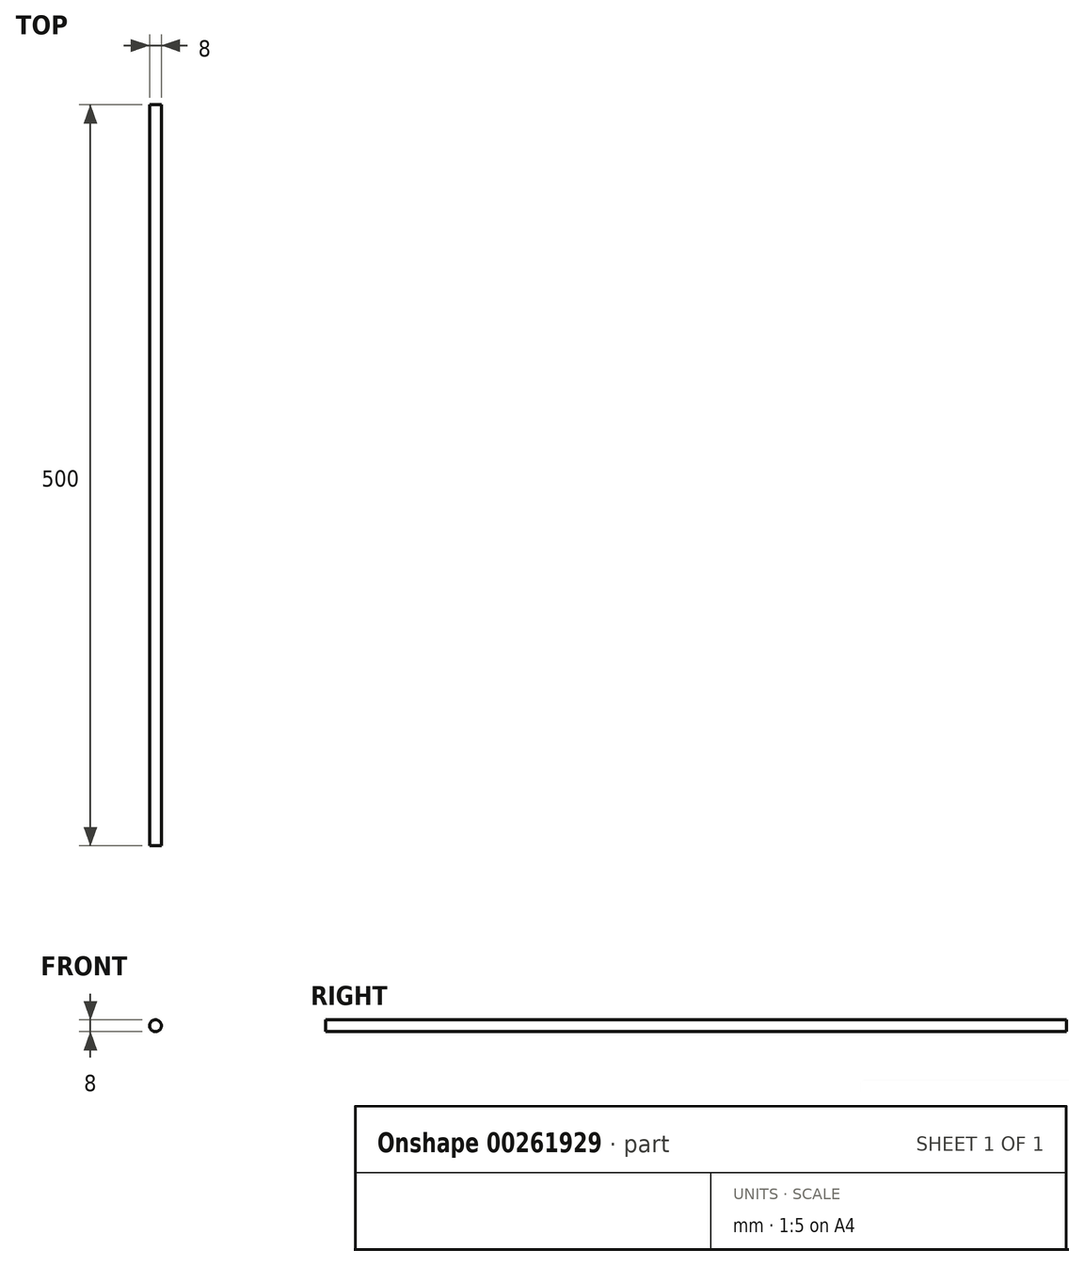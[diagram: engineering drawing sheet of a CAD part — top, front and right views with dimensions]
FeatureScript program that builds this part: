
annotation { "Feature Type Name" : "Feature", "Feature Type Description" : "" }
export const myFeature = defineFeature(function(context is Context, id is Id, definition is map)
    precondition{}
    {
        {
            var Q0;
            Q0=qCreatedBy(makeId("Front.planeOp"),FACE);
            var sketch = newSketch(context, id + "F0", { "sketchPlane" : qUnion([Q0])});
            skCircle(sketch, "E0", {"center": v(0, 0) * mm, "radius": 4 * mm});
            skSolve(sketch);
        }
        {
            var Q0;
            Q0=qSketchRegion(id+"F0",true);
            extrude(context, id + "F1", {"entities" : qUnion([Q0]), "depth" : 500 * mm});
        }
    });
